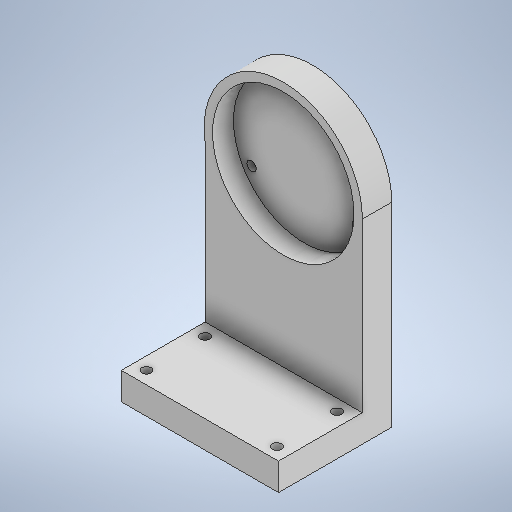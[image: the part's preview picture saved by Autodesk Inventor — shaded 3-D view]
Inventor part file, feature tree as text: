
AUTODESK INVENTOR PART (.ipt)
format: ipt  version: 2025 (Build 290162000, 162)  size: 285,184 bytes
history: native  units: mm
features: extrude x6, sketch x4, projected_geometry x1
ambient origin geometry x8: Origin, YZ Plane, XZ Plane, XY Plane, X Axis, Y Axis, Z Axis, Center Point
bodies: 实体1 (feature_tree)
feature tree (11):
  sketch  "草图1"  dims[d0=67.5mm d1=58.0mm]
  extrude  "拉伸1"  Depth=58.0mm
  extrude  "拉伸2"  Depth=30.0mm TaperAngle=360.0deg
  extrude  "拉伸3"  Depth=75.0mm
  extrude  "拉伸4"  Depth=13.0mm TaperAngle=0.0deg
  extrude  "拉伸5"  Depth=4.0mm
  extrude  "拉伸6"  Depth=13.0mm
  sketch  "草图 - 环形阵列1"  dims[d2=4.5mm d3=30.0mm d5=360.0deg]
  sketch  "草图2"  dims[d7=4.0mm d8=75.0mm]
  sketch  "草图3"  dims[d9=10.0mm d10=80.0mm d11=0.0mm d12=4.0mm d13=47.0mm d14=10.0mm d15=0.0mm d16=10.0mm d17=0.0mm d18=4.0mm d19=0.0mm d20=10.0mm d21=0.0mm d22=50.0mm d23=13.0mm d24=0.0mm d25=4.5mm d26=6.0mm d27=6.0mm]
  projected_geometry  "投影回路1"
